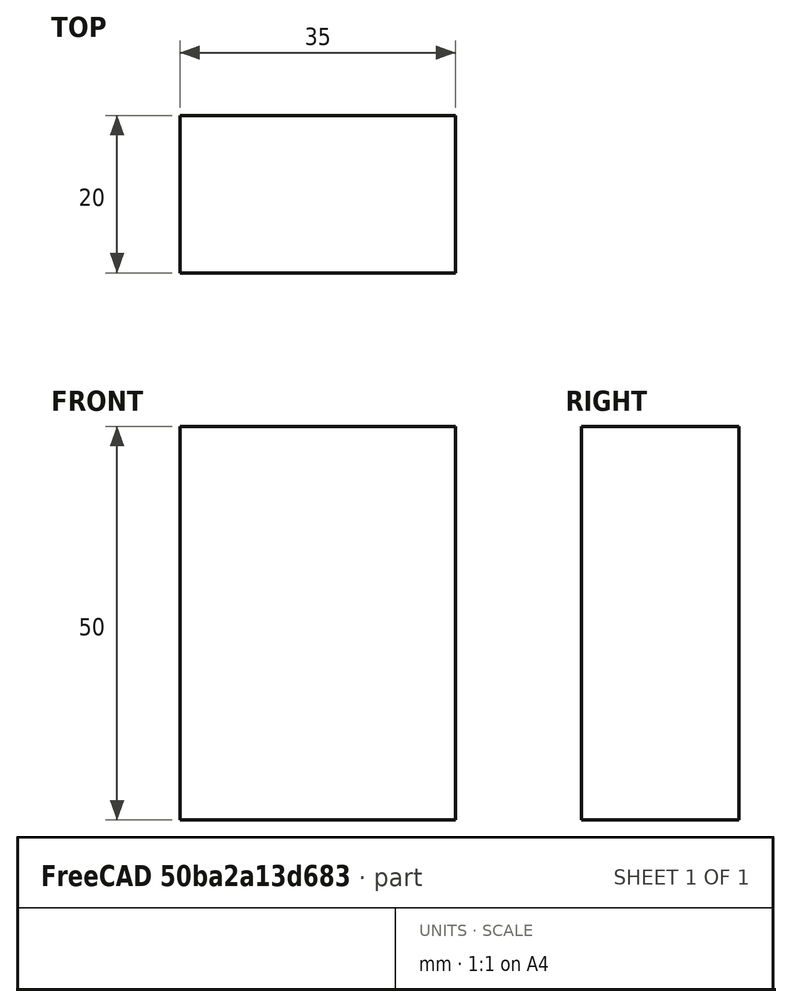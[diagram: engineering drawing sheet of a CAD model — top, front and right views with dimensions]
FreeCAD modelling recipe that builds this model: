
FCSTD DOCUMENT  (FreeCAD 0.15R4671 (Git))
Label: Flat Bar 35x20 EN10058 S235JR
License: All rights reserved
LicenseURL: http://en.wikipedia.org/wiki/All_rights_reserved
objects: Sketcher::SketchObject×1, Part::Extrusion×1
note: 2 computed .brp shape members not serialized (recipe doc carries the construction recipe); baked Part::Feature solids carry a one-line shape summary decoded from their .brp

FEATURE [Sketcher::SketchObject] Sketch
  sketch-geometry (4):
    g0: LineSegment StartX=-17.5 StartY=-10 StartZ=0 EndX=17.5 EndY=-10 EndZ=0
    g1: LineSegment StartX=17.5 StartY=-10 StartZ=0 EndX=17.5 EndY=10 EndZ=0
    g2: LineSegment StartX=17.5 StartY=10 StartZ=0 EndX=-17.5 EndY=10 EndZ=0
    g3: LineSegment StartX=-17.5 StartY=10 StartZ=0 EndX=-17.5 EndY=-10 EndZ=0
  constraints (12):
    c: Coincident(g0,g1)
    c: Coincident(g1,g2)
    c: Coincident(g2,g3)
    c: Coincident(g3,g0)
    c: Horizontal(g0)
    c: Horizontal(g2)
    c: Vertical(g1)
    c: Vertical(g3)
    c: Symmetric(g1,g2,g-2)
    c: Symmetric(g0,g1,g-1)
    c: DistanceY(g1) = 20
    c: DistanceX(g0) = 35
FEATURE [Part::Extrusion] Extrude  label="Flat Bar 35x20 EN10058 S235JR"
  Base = -> Sketch
  Dir = (0,0,50)
  Solid = true
